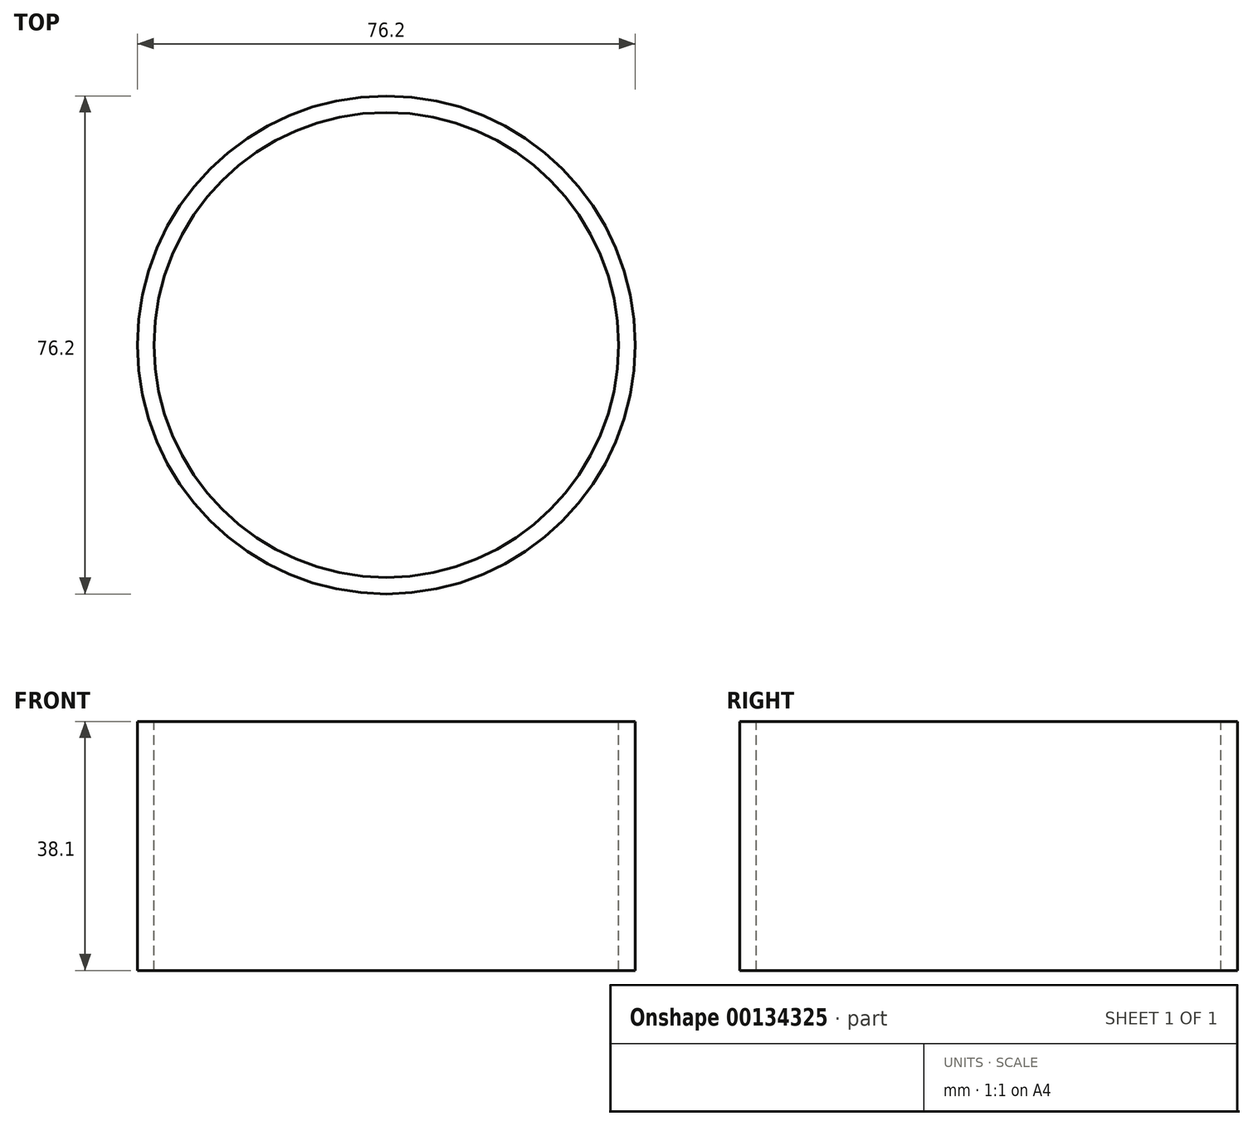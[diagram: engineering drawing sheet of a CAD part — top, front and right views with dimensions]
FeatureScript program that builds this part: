
annotation { "Feature Type Name" : "Feature", "Feature Type Description" : "" }
export const myFeature = defineFeature(function(context is Context, id is Id, definition is map)
    precondition{}
    {
        {
            var Q0;
            Q0=qCreatedBy(makeId("Top.planeOp"),FACE);
            var sketch = newSketch(context, id + "F0", { "sketchPlane" : qUnion([Q0])});
            skCircle(sketch, "E0", {"center": v(0, 0) * mm, "radius": 38.1 * mm});
            skCircle(sketch, "E1", {"center": v(0, 0) * mm, "radius": 35.56 * mm});
            skSolve(sketch);
        }
        {
            var Q0;
            Q0 = qConstructionFilter(qBodyType(qCreatedBy(id + "F0" ,EDGE), BodyType.WIRE), ConstructionObject.NO);
            extrude(context, id + "F1", {"bodyType" : ToolBodyType.SURFACE, "surfaceEntities" : qUnion([Q0]), "depth" : 38.1 * mm});
        }
        {
            var Q0;
            Q0=qCreatedBy(makeId("Top.planeOp"),FACE);
            cPlane(context, id + "F2", {"entities" : qUnion([Q0]), "cplaneType" : CPlaneType.OFFSET, "offset" : 25.4 * mm, "width" : 152.4 * mm, "height" : 152.4 * mm});
        }
    });
